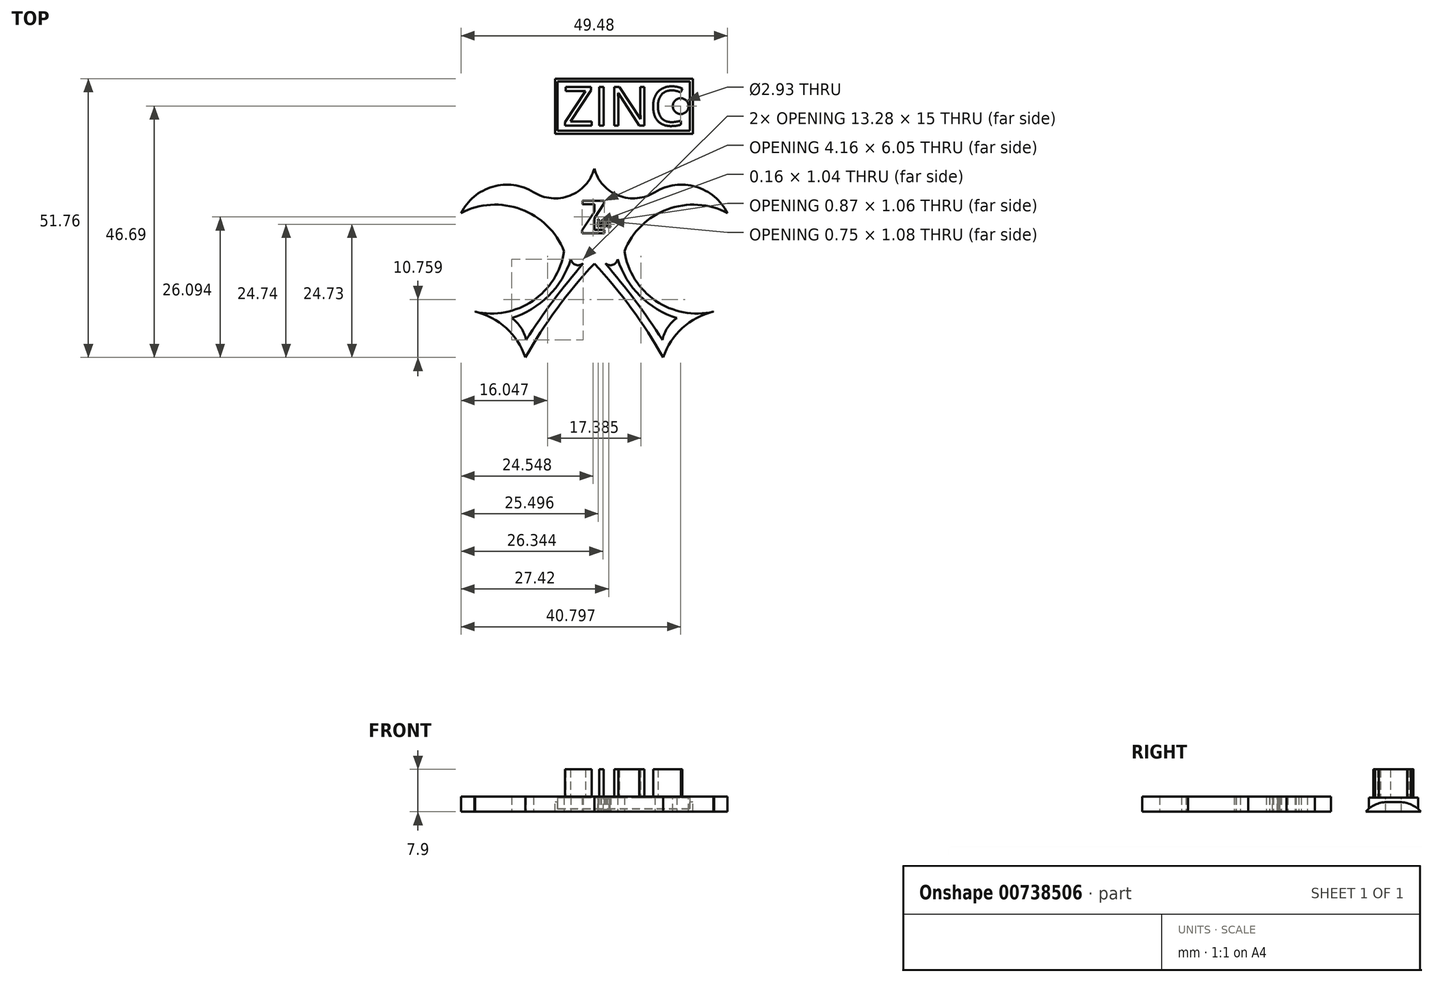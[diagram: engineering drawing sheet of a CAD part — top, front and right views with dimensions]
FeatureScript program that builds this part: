
annotation { "Feature Type Name" : "Feature", "Feature Type Description" : "" }
export const myFeature = defineFeature(function(context is Context, id is Id, definition is map)
    precondition{}
    {
        {
            var Q0;
            Q0=qCreatedBy(makeId("Top.planeOp"),FACE);
            var sketch = newSketch(context, id + "F0", { "sketchPlane" : qUnion([Q0])});
            skArc(sketch, "E0", {"start": v(-11.28, 3.89) * mm, "mid": v(-4.54, 3.22) * mm, "end": v(0, 8.25) * mm});
            skArc(sketch, "E1", {"start": v(-11.28, 3.89) * mm, "mid": v(-18.86, 4.88) * mm, "end": v(-24.74, 0) * mm});
            skArc(sketch, "E2", {"start": v(-5.6, -7.1) * mm, "mid": v(-13.6, 0.69) * mm, "end": v(-24.74, 0) * mm});
            skArc(sketch, "E3", {"start": v(-22.28, -18.3) * mm, "mid": v(-11.49, -16.35) * mm, "end": v(-5.6, -7.1) * mm});
            skArc(sketch, "E4", {"start": v(-12.8, -26.83) * mm, "mid": v(-16.43, -21.33) * mm, "end": v(-22.28, -18.3) * mm});
            skArc(sketch, "E5", {"start": v(0, -9.39) * mm, "mid": v(-6.91, -17.73) * mm, "end": v(-12.8, -26.83) * mm});
            skLineSegment(sketch, "E6", {"start": v(0, 8.25) * mm, "end": v(0, -9.39) * mm});
            skArc(sketch, "E7.MirrorCS", {"start": v(5.6, -7.1) * mm, "mid": v(13.6, 0.69) * mm, "end": v(24.74, 0) * mm});
            skArc(sketch, "E8.MirrorCS", {"start": v(11.28, 3.89) * mm, "mid": v(4.54, 3.22) * mm, "end": v(0, 8.25) * mm});
            skArc(sketch, "E9.MirrorCS", {"start": v(11.28, 3.89) * mm, "mid": v(18.86, 4.88) * mm, "end": v(24.74, 0) * mm});
            skArc(sketch, "E10.MirrorCS", {"start": v(0, -9.39) * mm, "mid": v(6.91, -17.73) * mm, "end": v(12.8, -26.83) * mm});
            skArc(sketch, "E11.MirrorCS", {"start": v(22.28, -18.3) * mm, "mid": v(11.49, -16.35) * mm, "end": v(5.6, -7.1) * mm});
            skArc(sketch, "E12.MirrorCS", {"start": v(12.8, -26.83) * mm, "mid": v(16.43, -21.33) * mm, "end": v(22.28, -18.3) * mm});
            skText(sketch, "E13", { "text": "Z\n", "fontName": "OpenSans-Regular.ttf"});
            skText(sketch, "E14", { "text": "inc\n", "fontName": "OpenSans-Regular.ttf"});
            skArc(sketch, "E15", {"start": v(4.35, -8.57) * mm, "mid": v(8.5, -15.38) * mm, "end": v(15.33, -19.5) * mm});
            skArc(sketch, "E16", {"start": v(15.33, -19.5) * mm, "mid": v(13.61, -21.29) * mm, "end": v(12.66, -23.57) * mm});
            skArc(sketch, "E17", {"start": v(12.66, -23.57) * mm, "mid": v(7.6, -16.28) * mm, "end": v(2.05, -9.34) * mm});
            skArc(sketch, "E18", {"start": v(2.05, -9.34) * mm, "mid": v(3.43, -9.63) * mm, "end": v(4.35, -8.57) * mm});
            skArc(sketch, "E19.MirrorCS", {"start": v(-15.33, -19.5) * mm, "mid": v(-13.61, -21.29) * mm, "end": v(-12.66, -23.57) * mm});
            skArc(sketch, "E20.MirrorCS", {"start": v(-4.35, -8.57) * mm, "mid": v(-8.5, -15.38) * mm, "end": v(-15.33, -19.5) * mm});
            skArc(sketch, "E21.MirrorCS", {"start": v(-12.66, -23.57) * mm, "mid": v(-7.6, -16.28) * mm, "end": v(-2.05, -9.34) * mm});
            skArc(sketch, "E22.MirrorCS", {"start": v(-2.05, -9.34) * mm, "mid": v(-3.43, -9.63) * mm, "end": v(-4.35, -8.57) * mm});
            const initialGuessF0  = {"E13": [-0.00261, -0.00376, 1, 0, 0.0061], "E14": [0.00051, -0.00262, 1, 0, 0.0014]};
            skSetInitialGuess(sketch, initialGuessF0);
            skSolve(sketch);
        }
        {
            var Q0;
            Q0 = qSketchRegion(id + "F0", true);
            extrude(context, id + "F1", {"entities" : qUnion([Q0]), "depth" : 2.82 * mm, "offsetDistance" : 25.4 * mm});
        }
        {
            var Q0;
            Q0=qCreatedBy(makeId("Top.planeOp"),FACE);
            var sketch = newSketch(context, id + "F2", { "sketchPlane" : qUnion([Q0])});
            skLineSegment(sketch, "E23.bottom", {"start": v(-7.3, 24.93) * mm, "end": v(18.3, 24.93) * mm});
            skLineSegment(sketch, "E23.top", {"start": v(-7.3, 14.7) * mm, "end": v(18.3, 14.7) * mm});
            skLineSegment(sketch, "E23.left", {"start": v(-7.3, 24.93) * mm, "end": v(-7.3, 14.7) * mm});
            skLineSegment(sketch, "E23.right", {"start": v(18.3, 24.93) * mm, "end": v(18.3, 14.7) * mm});
            skSolve(sketch);
        }
        {
            var Q0;
            Q0 = qSketchRegion(id + "F2", true);
            extrude(context, id + "F3", {"entities" : qUnion([Q0]), "depth" : 1.78 * mm, "offsetDistance" : 25.4 * mm});
        }
        {
            var Q0;
            Q0=makeQuery(id+"F3.opExtrude","CAP_FACE",FACE,{"disambiguationData":[OSD([sQuery(id+"F2.wireOp",EDGE,"E23.bottom"),sQuery(id+"F2.wireOp",EDGE,"E23.top"),sQuery(id+"F2.wireOp",EDGE,"E23.left"),sQuery(id+"F2.wireOp",EDGE,"E23.right")])],"isStart":false});
            var sketch = newSketch(context, id + "F4", { "sketchPlane" : qUnion([Q0])});
            skLineSegment(sketch, "E24.bottom", {"start": v(-6.8, 24.41) * mm, "end": v(17.76, 24.41) * mm});
            skLineSegment(sketch, "E24.top", {"start": v(-6.8, 15.3) * mm, "end": v(17.76, 15.3) * mm});
            skLineSegment(sketch, "E24.left", {"start": v(-6.8, 24.41) * mm, "end": v(-6.8, 15.3) * mm});
            skLineSegment(sketch, "E24.right", {"start": v(17.76, 24.41) * mm, "end": v(17.76, 15.3) * mm});
            skSolve(sketch);
        }
        {
            var Q0;
            Q0=makeQuery(id+"F4.imprint","IMPRINT",FACE,{"disambiguationData":[TD([[makeQuery(id+"F4.imprint","IMPRINT",EDGE,{"derivedFrom":sQuery(id+"F4.wireOp",EDGE,"E24.bottom")}),-1.0]])]});
            extrude(context, id + "F5", {"entities" : qUnion([Q0]), "operationType" : NewBodyOperationType.ADD, "depth" : 0.86 * mm, "offsetDistance" : 25.4 * mm});
        }
        {
            var Q0;
            Q0=makeQuery(id+"F3.opExtrude","CAP_EDGE",EDGE,{"disambiguationData":[OSD([sQuery(id+"F2.wireOp",EDGE,"E23.top")])],"isStart":false});
            var Q1;
            Q1=makeQuery(id+"F3.opExtrude","CAP_EDGE",EDGE,{"disambiguationData":[OSD([sQuery(id+"F2.wireOp",EDGE,"E23.bottom")])],"isStart":false});
            fillet(context, id + "F6", {"entities" : qUnion([Q0, Q1]), "radius" : 5.08 * mm, "tangentPropagation" : true, "allowEdgeOverflow" : false});
        }
        {
            var Q0;
            Q0=makeQuery(id+"F5.opExtrude","CAP_FACE",FACE,{"disambiguationData":[OSD([sQuery(id+"F4.wireOp",EDGE,"E24.bottom"),sQuery(id+"F4.wireOp",EDGE,"E24.top"),sQuery(id+"F4.wireOp",EDGE,"E24.left"),sQuery(id+"F4.wireOp",EDGE,"E24.right")])],"isStart":false});
            var sketch = newSketch(context, id + "F7", { "sketchPlane" : qUnion([Q0])});
            skCircle(sketch, "E25", {"center": v(16.06, 19.86) * mm, "radius": 1.46 * mm});
            skPoint(sketch, "E25.centerSnap0", {"position": v(17.76, 19.86) * mm});
            skSolve(sketch);
        }
        {
            var Q0;
            Q0 = qSketchRegion(id + "F7", true);
            extrude(context, id + "F8", {"entities" : qUnion([Q0]), "operationType" : NewBodyOperationType.REMOVE, "oppositeDirection" : true, "depth" : 25.4 * mm, "offsetDistance" : 25.4 * mm});
        }
        {
            var Q0;
            Q0=makeQuery(id+"F5.opExtrude","CAP_FACE",FACE,{"disambiguationData":[OSD([sQuery(id+"F4.wireOp",EDGE,"E24.bottom"),sQuery(id+"F4.wireOp",EDGE,"E24.top"),sQuery(id+"F4.wireOp",EDGE,"E24.left"),sQuery(id+"F4.wireOp",EDGE,"E24.right")])],"isStart":false});
            var sketch = newSketch(context, id + "F9", { "sketchPlane" : qUnion([Q0])});
            skText(sketch, "E26", { "text": "ZINC", "fontName": "OpenSans-Regular.ttf"});
            const initialGuessF9  = {"E26": [-0.00583, 0.01624, 1, 0, 0.00725]};
            skSetInitialGuess(sketch, initialGuessF9);
            skSolve(sketch);
        }
        {
            var Q0;
            Q0 = qSketchRegion(id + "F9", true);
            extrude(context, id + "F10", {"entities" : qUnion([Q0]), "operationType" : NewBodyOperationType.ADD, "depth" : 5.26 * mm, "offsetDistance" : 25.4 * mm});
        }
    });
